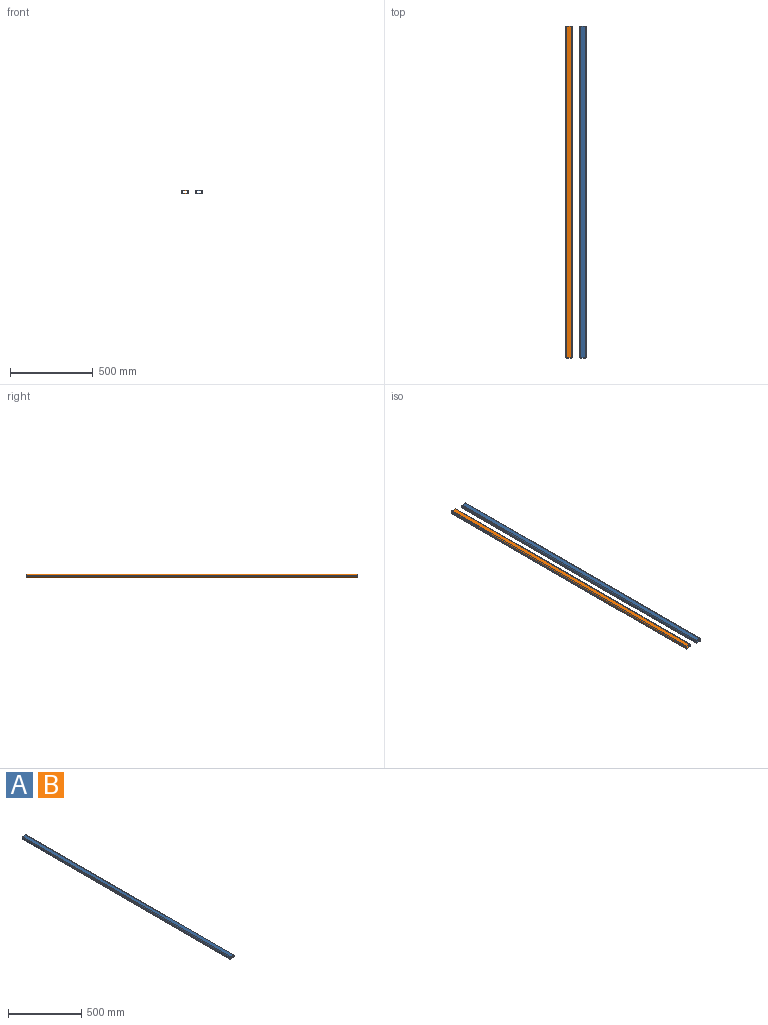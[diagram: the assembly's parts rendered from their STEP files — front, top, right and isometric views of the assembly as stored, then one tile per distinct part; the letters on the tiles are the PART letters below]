
ASSEMBLY  parts=2 mates=2
PART A: 18 faces, bbox 40x2000x20 mm
  f0: plane 2000x30mm, normal (0,0,1), area 60000mm2, adj f8,f9,f14,f17
  f1: plane 2000x10mm, normal (-1,0,0), area 20000mm2, adj f8,f9,f14,f15
  f2: plane 2000x30mm, normal (0,0,-1), area 60000mm2, adj f8,f9,f15,f16
  f3: plane 2000x6mm, normal (1,0,0), area 12000mm2, adj f8,f9,f10,f13
  f4: plane 2000x26mm, normal (0,0,-1), area 52000mm2, adj f8,f9,f10,f11
  f5: plane 2000x6mm, normal (-1,0,0), area 12000mm2, adj f8,f9,f11,f12
  f6: plane 2000x26mm, normal (0,0,1), area 52000mm2, adj f8,f9,f12,f13
  f7: plane 2000x10mm, normal (1,0,0), area 20000mm2, adj f8,f9,f16,f17
  f8: plane 40x20mm, normal (0,-1,0), area 224mm2, adj f0,f1,f2,f3,f4,f5,f6,f7
  f9: plane 40x20mm, normal (0,1,0), area 224mm2, adj f0,f1,f2,f3,f4,f5,f6,f7
  f10: cylinder r=5mm len=2000mm, axis (0,1,0), area 15708mm2, adj f3,f4,f8,f9
  f11: cylinder r=5mm len=2000mm, axis (0,-1,0), area 15708mm2, adj f4,f5,f8,f9
  f12: cylinder r=5mm len=2000mm, axis (0,1,0), area 15708mm2, adj f5,f6,f8,f9
  f13: cylinder r=5mm len=2000mm, axis (0,-1,0), area 15708mm2, adj f3,f6,f8,f9
  f14: cylinder r=5mm len=2000mm, axis (0,-1,0), area 15708mm2, adj f0,f1,f8,f9
  f15: cylinder r=5mm len=2000mm, axis (0,1,0), area 15708mm2, adj f1,f2,f8,f9
  f16: cylinder r=5mm len=2000mm, axis (0,-1,0), area 15708mm2, adj f2,f7,f8,f9
  f17: cylinder r=5mm len=2000mm, axis (0,1,0), area 15708mm2, adj f0,f7,f8,f9
PART B: same geometry as A
PLACE A t=(45.63,2000,6.3)mm
PLACE B t=(-39.37,2000,6.3)mm
MATE fastened B.f8 <-> A.f8  axis (0,-1,0) through (-19.37,0,6.3)mm
MATE planar A.f8 <-> A.f8  axis (0,-1,0) through (45.63,0,6.3)mm
